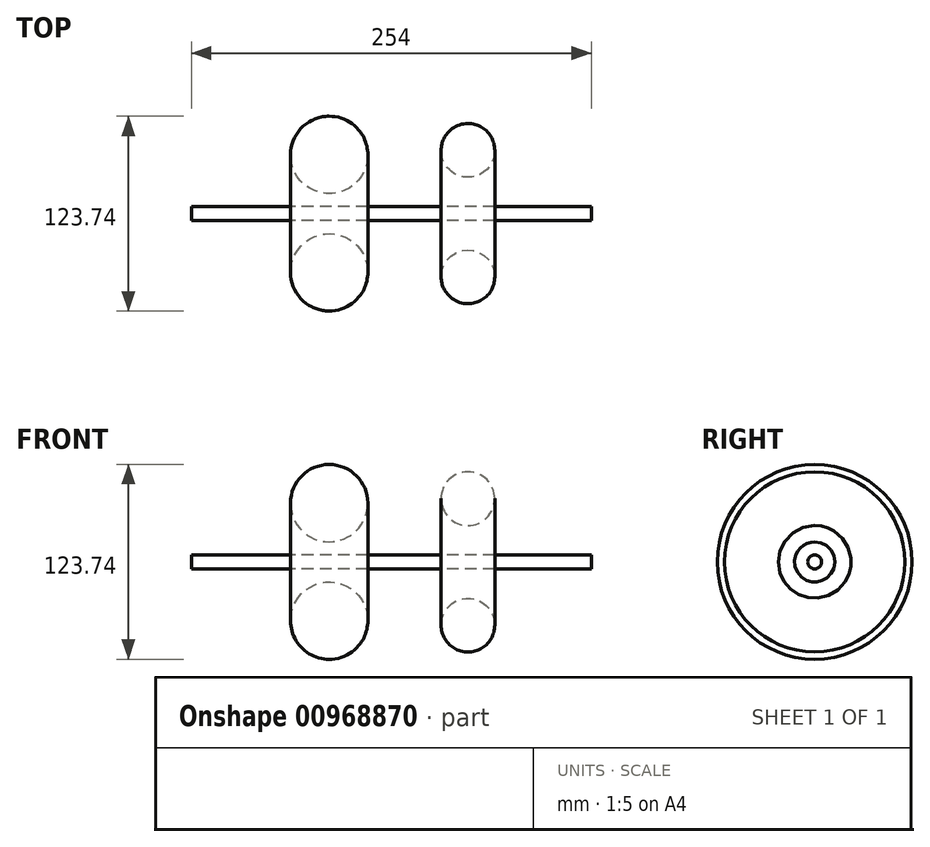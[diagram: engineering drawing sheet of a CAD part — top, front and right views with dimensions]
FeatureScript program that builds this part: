
annotation { "Feature Type Name" : "Feature", "Feature Type Description" : "" }
export const myFeature = defineFeature(function(context is Context, id is Id, definition is map)
    precondition{}
    {
        {
            var Q0;
            Q0=qCreatedBy(makeId("Top.planeOp"),FACE);
            var sketch = newSketch(context, id + "F0", { "sketchPlane" : qUnion([Q0])});
            skCircle(sketch, "E0", {"center": v(-39.48, 37.31) * mm, "radius": 24.56 * mm});
            skCircle(sketch, "E1", {"center": v(48.66, -40.16) * mm, "radius": 17.05 * mm});
            skSolve(sketch);
        }
        {
            var Q0;
            Q0 = qSketchRegion(id + "F0", true);
            var sketch = newSketch(context, id + "F1", { "sketchPlane" : qUnion([Q0])});
            skLineSegment(sketch, "E2", {"start": v(-64.62, 0) * mm, "end": v(68.76, 0) * mm, "construction": true});
            skSolve(sketch);
        }
        {
            var Q0;
            Q0 = qSketchRegion(id + "F0", true);
            var Q1;
            Q1=sQuery(id+"F1.wireOp",EDGE,"E2");
            revolve(context, id + "F2", {"surfaceOperationType" : NewSurfaceOperationType.NEW, "entities" : qUnion([Q0]), "axis" : qUnion([Q1]), "revolveType" : RevolveType.FULL});
        }
        {
            var Q0;
            Q0=qCreatedBy(makeId("Right.planeOp"),FACE);
            var sketch = newSketch(context, id + "F3", { "sketchPlane" : qUnion([Q0])});
            skCircle(sketch, "E3", {"center": v(0, 0) * mm, "radius": 4.44 * mm});
            skSolve(sketch);
        }
        {
            var Q0;
            Q0 = qSketchRegion(id + "F3", true);
            extrude(context, id + "F4", {"entities" : qUnion([Q0]), "endBound" : BoundingType.SYMMETRIC, "depth" : 254 * mm, "offsetDistance" : 25.4 * mm});
        }
    });
